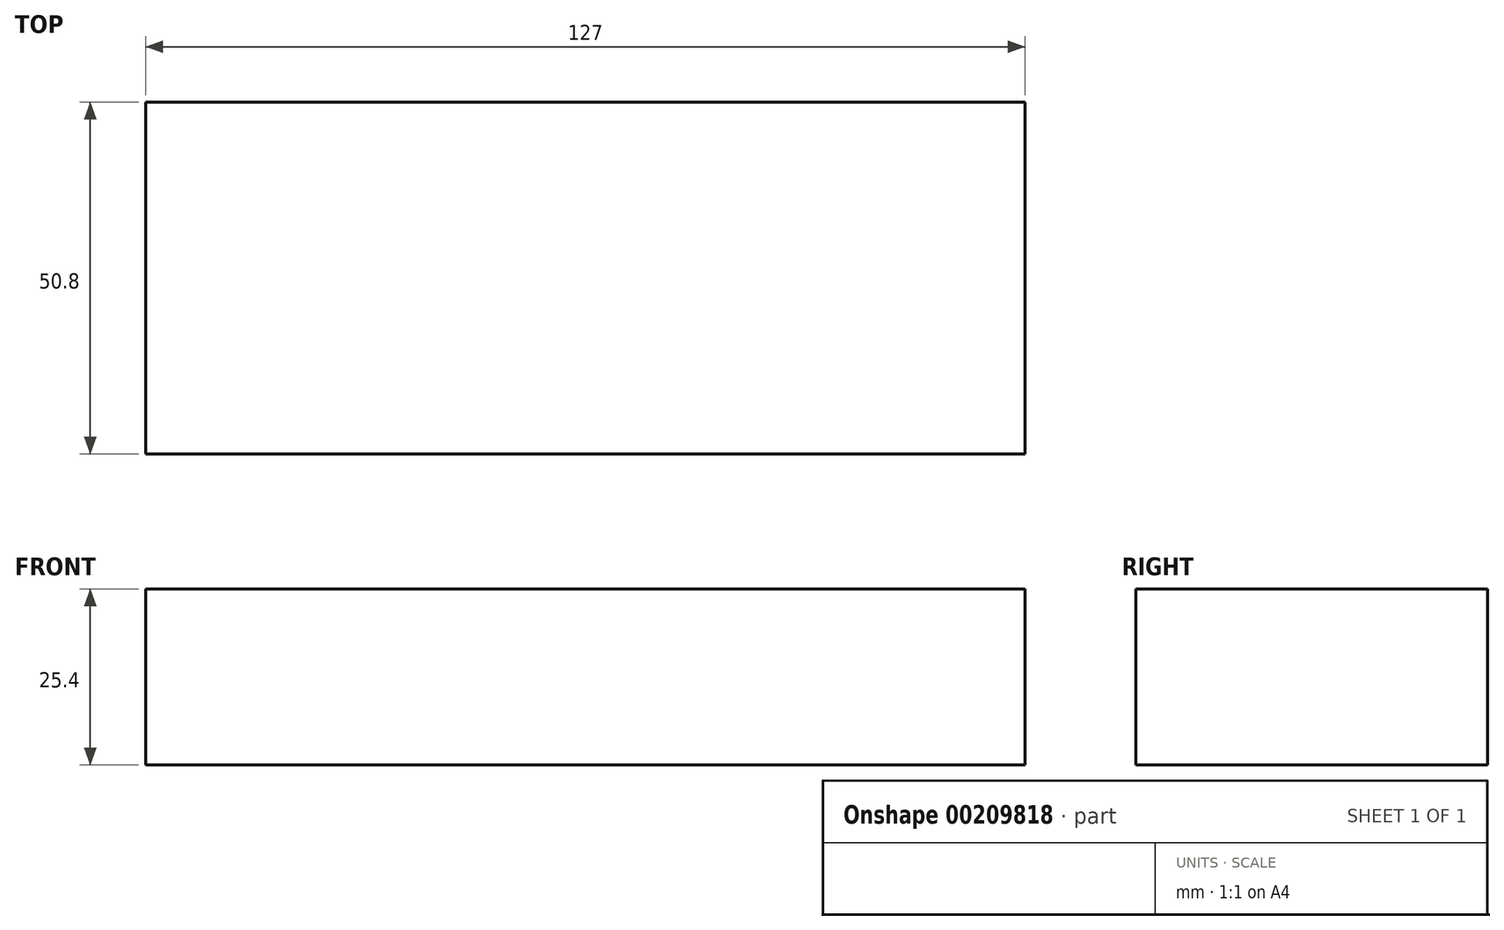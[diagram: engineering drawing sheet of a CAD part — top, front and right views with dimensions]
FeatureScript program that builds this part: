
annotation { "Feature Type Name" : "Feature", "Feature Type Description" : "" }
export const myFeature = defineFeature(function(context is Context, id is Id, definition is map)
    precondition{}
    {
        {
            var Q0;
            Q0=qCreatedBy(makeId("Top.planeOp"),FACE);
            var sketch = newSketch(context, id + "F0", { "sketchPlane" : qUnion([Q0])});
            skLineSegment(sketch, "E0.bottom", {"start": v(63.5, 25.4) * mm, "end": v(-63.5, 25.4) * mm});
            skLineSegment(sketch, "E0.top", {"start": v(63.5, -25.4) * mm, "end": v(-63.5, -25.4) * mm});
            skLineSegment(sketch, "E0.left", {"start": v(63.5, 25.4) * mm, "end": v(63.5, -25.4) * mm});
            skLineSegment(sketch, "E0.right", {"start": v(-63.5, 25.4) * mm, "end": v(-63.5, -25.4) * mm});
            skPoint(sketch, "E0.middle", {"position": v(0, 0) * mm});
            skSolve(sketch);
        }
        {
            var Q0;
            Q0 = qSketchRegion(id + "F0", true);
            extrude(context, id + "F1", {"entities" : qUnion([Q0]), "depth" : 25.4 * mm});
        }
    });
